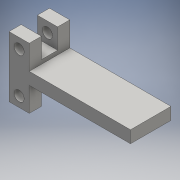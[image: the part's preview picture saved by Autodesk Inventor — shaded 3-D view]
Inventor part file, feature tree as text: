
AUTODESK INVENTOR PART (.ipt)
format: ipt  version: 2016 (Build 200138000, 138)  size: 154,112 bytes
history: native  units: mm
features: extrude x8, sketch x8, other x1
ambient origin geometry x8: Origin, YZ Plane, XZ Plane, XY Plane, X Axis, Y Axis, Z Axis, Center Point
bodies: Body1 (feature_tree)
feature tree (17):
  other  "ソリッド1"
  extrude  "押し出し1"  Depth=30.0mm
  extrude  "押し出し2"  Depth=15.0mm
  extrude  "押し出し3"  Depth=10.0mm TaperAngle=0.0deg
  extrude  "押し出し4"  Depth=25.0mm
  extrude  "押し出し5"  Depth=6.0mm
  extrude  "押し出し6"  Depth=5.0mm
  extrude  "押し出し7"  Depth=10.0mm TaperAngle=0.0deg
  extrude  "押し出し8"  Depth=25.0mm
  sketch  "スケッチ1"
  sketch  "スケッチ2"
  sketch  "スケッチ3"
  sketch  "スケッチ4"
  sketch  "スケッチ6"
  sketch  "スケッチ7"
  sketch  "スケッチ8"
  sketch  "スケッチ9"
